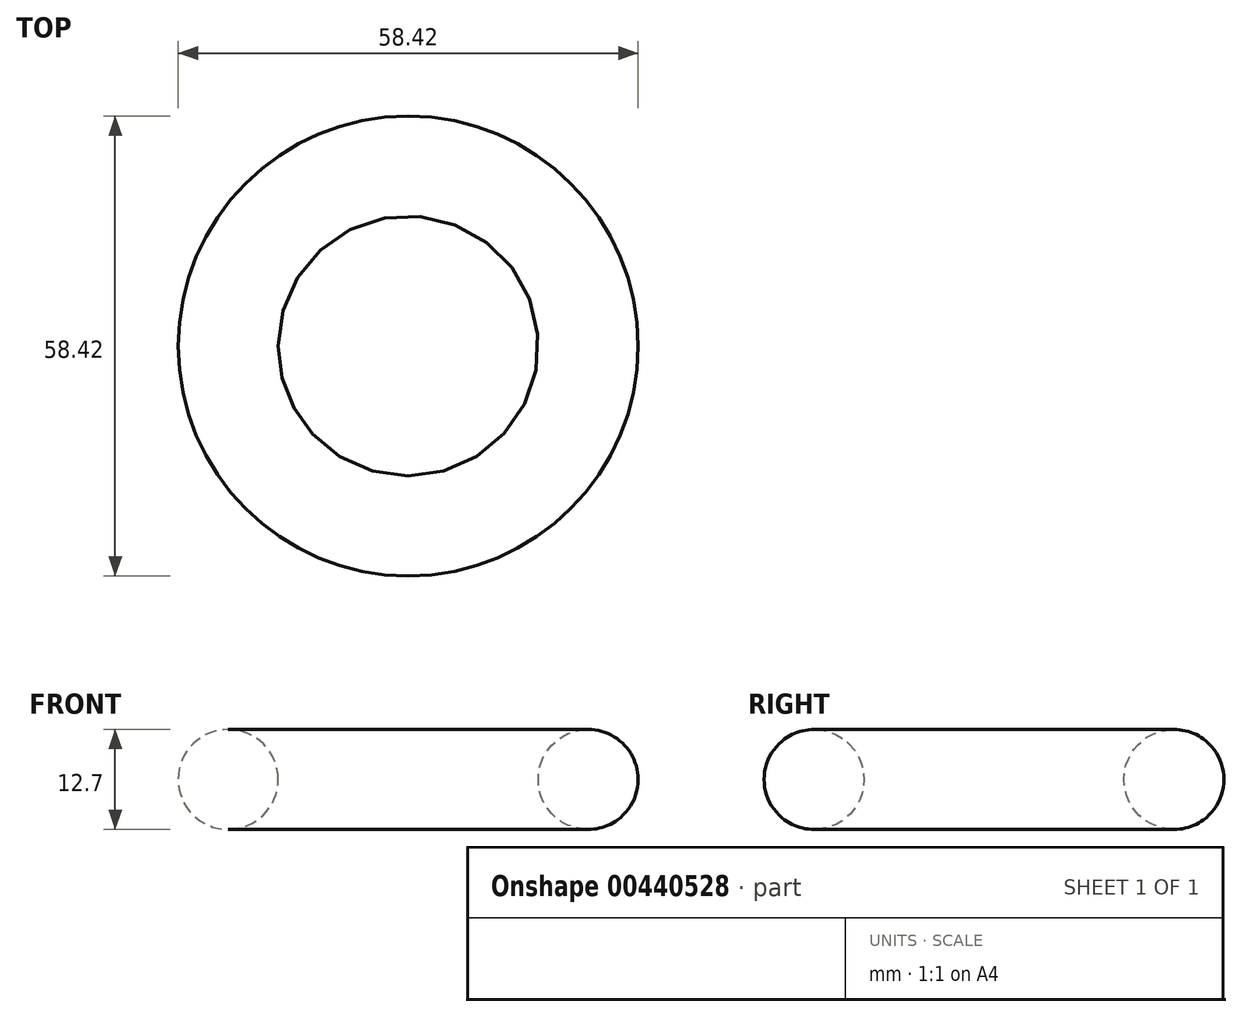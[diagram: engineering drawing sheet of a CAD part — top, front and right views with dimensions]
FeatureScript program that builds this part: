
annotation { "Feature Type Name" : "Feature", "Feature Type Description" : "" }
export const myFeature = defineFeature(function(context is Context, id is Id, definition is map)
    precondition{}
    {
        {
            var Q0;
            Q0=qCreatedBy(makeId("Front.planeOp"),FACE);
            var sketch = newSketch(context, id + "F0", { "sketchPlane" : qUnion([Q0])});
            skCircle(sketch, "E0", {"center": v(22.86, 0) * mm, "radius": 6.35 * mm});
            skLineSegment(sketch, "E1", {"start": v(0, 0) * mm, "end": v(0, 15.88) * mm, "construction": true});
            skSolve(sketch);
        }
        {
            var Q0;
            Q0 = qSketchRegion(id + "F0", true);
            var Q1;
            Q1=sQuery(id+"F0.wireOp",EDGE,"E1");
            revolve(context, id + "F1", {"entities" : qUnion([Q0]), "axis" : qUnion([Q1]), "revolveType" : RevolveType.FULL});
        }
    });
